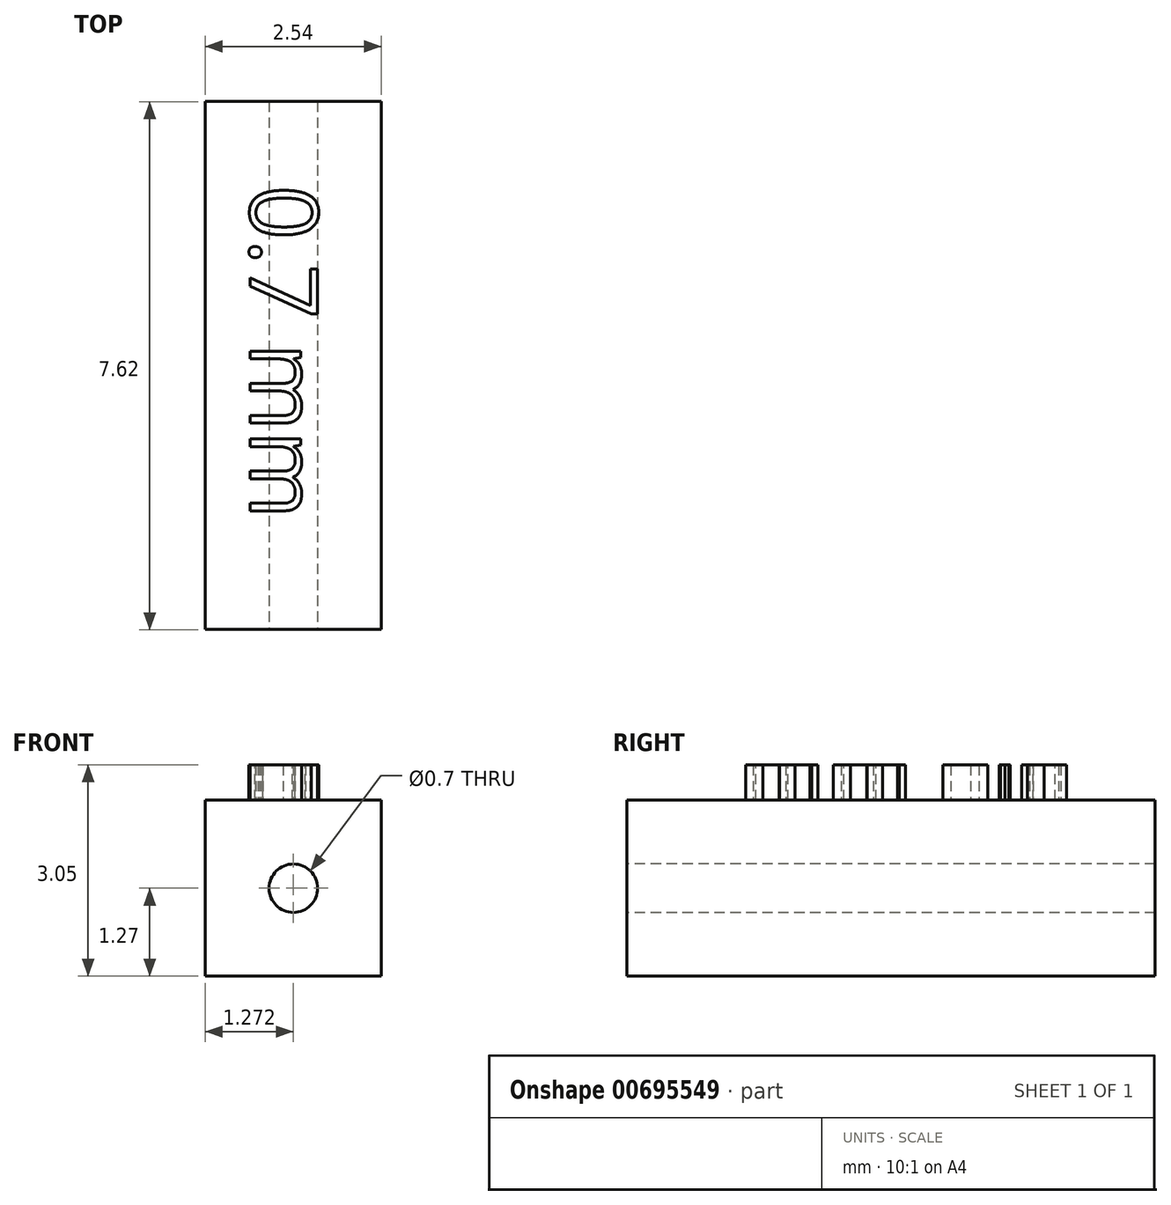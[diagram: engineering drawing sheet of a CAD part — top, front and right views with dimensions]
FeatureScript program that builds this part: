
annotation { "Feature Type Name" : "Feature", "Feature Type Description" : "" }
export const myFeature = defineFeature(function(context is Context, id is Id, definition is map)
    precondition{}
    {
        {
            var Q0;
            Q0=qCreatedBy(makeId("Top.planeOp"),FACE);
            var sketch = newSketch(context, id + "F0", { "sketchPlane" : qUnion([Q0])});
            skLineSegment(sketch, "E0.bottom", {"start": v(-2.43, 1.91) * mm, "end": v(0.11, 1.91) * mm});
            skLineSegment(sketch, "E0.top", {"start": v(-2.43, -5.7) * mm, "end": v(0.11, -5.7) * mm});
            skLineSegment(sketch, "E0.left", {"start": v(-2.43, 1.91) * mm, "end": v(-2.43, -5.7) * mm});
            skLineSegment(sketch, "E0.right", {"start": v(0.11, 1.91) * mm, "end": v(0.11, -5.7) * mm});
            skSolve(sketch);
        }
        {
            var Q0;
            Q0 = qSketchRegion(id + "F0", true);
            extrude(context, id + "F1", {"entities" : qUnion([Q0]), "depth" : 2.54 * mm, "offsetDistance" : 25.4 * mm});
        }
        {
            var Q0;
            Q0=makeQuery(id+"F1.opExtrude","SWEPT_FACE",FACE,{"disambiguationData":[OSD([sQuery(id+"F0.wireOp",EDGE,"E0.top")])]});
            var sketch = newSketch(context, id + "F2", { "sketchPlane" : qUnion([Q0])});
            skCircle(sketch, "E1", {"center": v(-1.16, 1.27) * mm, "radius": 0.35 * mm});
            skSolve(sketch);
        }
        {
            var Q0;
            Q0=makeQuery(id+"F2.imprint","IMPRINT",FACE,{"disambiguationData":[TD([[makeQuery(id+"F2.imprint","IMPRINT",EDGE,{"derivedFrom":sQuery(id+"F2.wireOp",EDGE,"E1")}),1.0]])]});
            var Q1;
            Q1=sQuery(id+"F2.wireOp",EDGE,"E1");
            extrude(context, id + "F3", {"entities" : qUnion([Q0]), "operationType" : NewBodyOperationType.REMOVE, "surfaceEntities" : qUnion([Q1]), "oppositeDirection" : true, "depth" : 7.62 * mm, "offsetDistance" : 25.4 * mm});
        }
        {
            var Q0;
            Q0=makeQuery(id+"F1.opExtrude","CAP_FACE",FACE,{"disambiguationData":[OSD([sQuery(id+"F0.wireOp",EDGE,"E0.bottom"),sQuery(id+"F0.wireOp",EDGE,"E0.top"),sQuery(id+"F0.wireOp",EDGE,"E0.left"),sQuery(id+"F0.wireOp",EDGE,"E0.right")])],"isStart":false});
            var sketch = newSketch(context, id + "F4", { "sketchPlane" : qUnion([Q0])});
            skSolve(sketch);
        }
        {
            var Q0;
            Q0=makeQuery(id+"F4.imprint","IMPRINT",FACE,{"disambiguationData":[TD([[makeQuery(id+"F4.imprint","IMPRINT",EDGE,{"derivedFrom":makeQuery(id+"F1.opExtrude","CAP_EDGE",EDGE,{"disambiguationData":[OSD([sQuery(id+"F0.wireOp",EDGE,"E0.bottom")])],"isStart":false})}),-1.0]])]});
            var sketch = newSketch(context, id + "F5", { "sketchPlane" : qUnion([Q0])});
            skText(sketch, "E2", { "text": "0.7 mm", "fontName": "OpenSans-Regular.ttf"});
            const initialGuessF5  = {"E2": [-0.00178, 0.0007, 0, -1, 0.00098]};
            skSetInitialGuess(sketch, initialGuessF5);
            skSolve(sketch);
        }
        {
            var Q0;
            Q0 = qSketchRegion(id + "F5", true);
            extrude(context, id + "F6", {"entities" : qUnion([Q0]), "operationType" : NewBodyOperationType.ADD, "depth" : 0.5 * mm, "offsetDistance" : 25.4 * mm});
        }
    });
